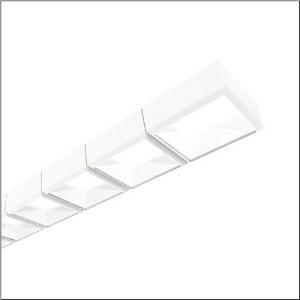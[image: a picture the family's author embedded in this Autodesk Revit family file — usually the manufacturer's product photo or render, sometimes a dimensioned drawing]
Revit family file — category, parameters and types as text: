
# Revit family: scriptus_r__11_5mz314d04wa_e059
name_source: partatom
category: Lighting Fixtures
units: mm (PartAtom-declared; Revit-internal decimal feet)

## family parameters
Cut with Voids When Loaded = No
Host = Face
Light Source = No
Part Type = Normal
Room Calculation Point = No
Round Connector Dimension = Use Diameter
Shared = No

## types (1)
- Scriptus® 11 (1 x LED 4000K / CRI = 80 (unbekannt), 3220 lm / 4820 lm, 4000K)
    Apparent Load = 120 VA
    CIE Flux Codes = - - - 0 100 / 82 95 99 100 100
    Color Rendering = 80
    Color Temperature = 4000K
    Default Elevation = 1800 mm
    Description = Scriptus® 11, office luminaire, primary optical cover: lenses, CAT 2 (L<= 3000cd/m²), light emission: direct/indirect distribution, primary light characteristic: symmetric, installation type: suspended mounting, LED rated luminous flux: 16.060 lm, light colour: 840, colour temperature: 4000K, control gear: ECG DALI, with terminal, 5-pole, mains connection: 230V, AC, 50Hz, rated input power: 120W, LED control gear: ECG DALI, housing, luminaire housing, of aluminium, traffic white (RAL 9016), length: 3.088 mm, width: 114 mm, height: 57mm, protection rating (complete): IP20, insulation class (complete): insulation class I (protective earthing), certification: CE, ENEC, VDE, protection symbol: F, permissible ambient temperature for indoor applications: 0..+35°C, standard: EN 50419, packaging unit: 1 piece
    Height = 57 mm
    Lamp = 1 x LED 4000K / CRI >= 80 (unbekannt)
    Lamp Light Flux = 3220 lm / 4820 lm
    Lamp count = 1
    Length = 3088 mm
    Luminous efficacy = 134 lm/W
    Manufacturer = Siteco
    ModVariant = No
    Model = 5MZ314D04WA
    Mounting Place = Ceiling
    Mounting Type = Pendant
    Number of Poles = 1
    OnlyDefault = Yes
    Power Factor = 1
    Product Name = Scriptus® 11
    Product group = office luminaire | ceiling pendant
    ProductGroupID = 905
    Protection Class = Protection class I
    Protection Degree = IP 20
    RLX_Detail_Level = 1
    RlxData = <blob elided: 31937 chars, md5=9966a9fe>
    Socket = socket
    Standby Power = 0 W
    System Light Flux = 16080 lm
    System Power = 120 W
    Type Comments = Product without accessories
    Type Image = l_1004839.jpg
    URL = http://relux.com
    VarID = ---
    Voltage = 0 V
    Weight = 0.00 kg
    Width = 114 mm

## geometry (parser evidence)
native form markers: Blend x4, Sweep x16
no freeform markers — native parametric forms only
